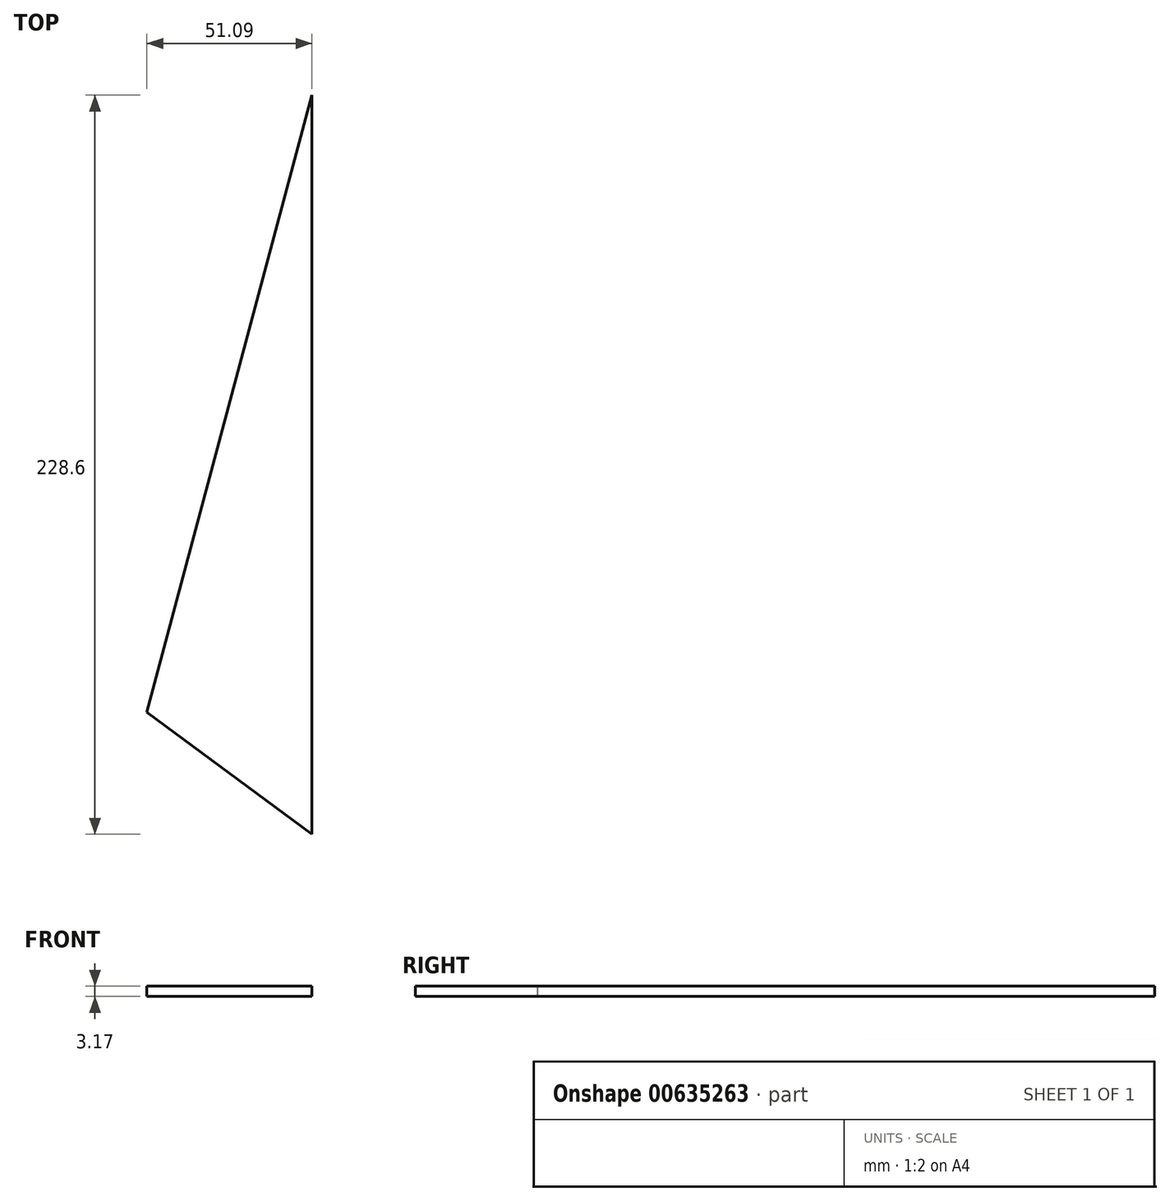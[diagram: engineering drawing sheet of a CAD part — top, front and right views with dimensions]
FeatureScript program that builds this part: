
annotation { "Feature Type Name" : "Feature", "Feature Type Description" : "" }
export const myFeature = defineFeature(function(context is Context, id is Id, definition is map)
    precondition{}
    {
        {
            var Q0;
            Q0=qCreatedBy(makeId("Top.planeOp"),FACE);
            var sketch = newSketch(context, id + "F0", { "sketchPlane" : qUnion([Q0])});
            skLineSegment(sketch, "E0", {"start": v(0, 0) * mm, "end": v(0, -228.6) * mm});
            skLineSegment(sketch, "E1", {"start": v(0, -228.6) * mm, "end": v(-51.1, -190.9) * mm});
            skLineSegment(sketch, "E2", {"start": v(-51.1, -190.9) * mm, "end": v(0, 0) * mm});
            skSolve(sketch);
        }
        {
            var Q0;
            Q0 = qSketchRegion(id + "F0", true);
            extrude(context, id + "F1", {"entities" : qUnion([Q0]), "depth" : 3.17 * mm, "offsetDistance" : 25.4 * mm});
        }
    });
